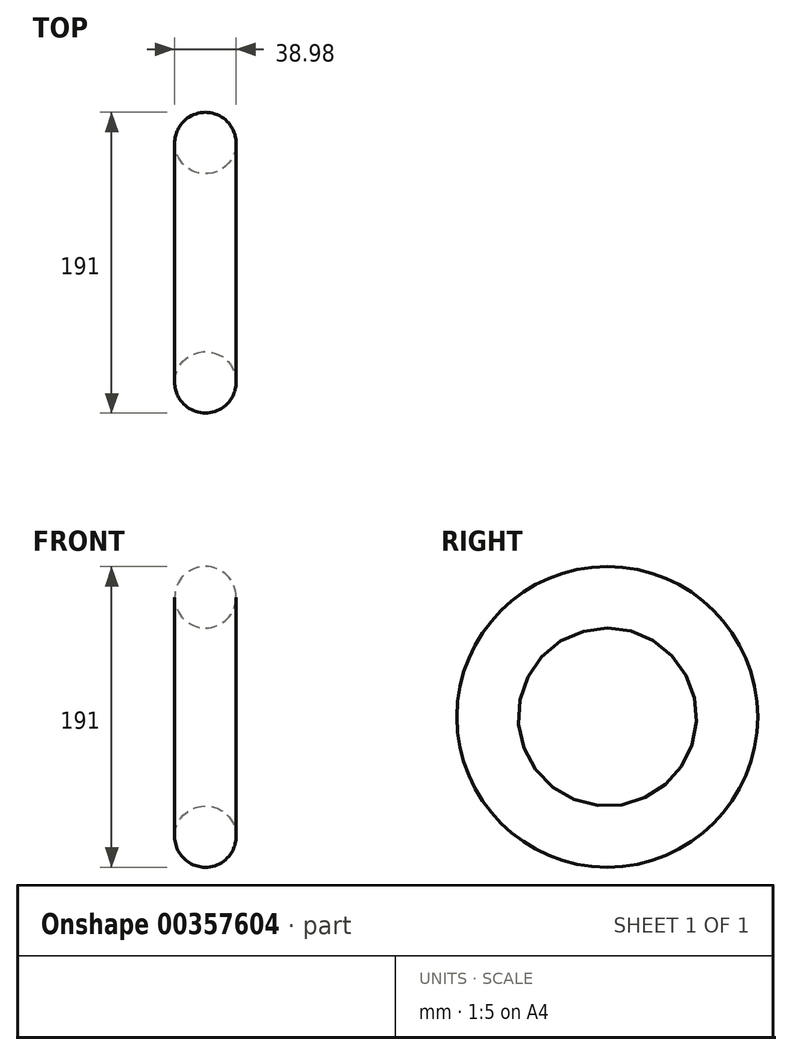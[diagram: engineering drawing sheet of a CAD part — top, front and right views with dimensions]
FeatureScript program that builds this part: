
annotation { "Feature Type Name" : "Feature", "Feature Type Description" : "" }
export const myFeature = defineFeature(function(context is Context, id is Id, definition is map)
    precondition{}
    {
        {
            var Q0;
            Q0=qCreatedBy(makeId("Front.planeOp"),FACE);
            var sketch = newSketch(context, id + "F0", { "sketchPlane" : qUnion([Q0])});
            skCircle(sketch, "E0", {"center": v(0, 0) * mm, "radius": 19.49 * mm});
            skLineSegment(sketch, "E1", {"start": v(-26.07, -76) * mm, "end": v(24.42, -76) * mm});
            skSolve(sketch);
        }
        {
            var Q0;
            Q0=makeQuery(id+"F0.imprint","IMPRINT",FACE,{"disambiguationData":[TD([[makeQuery(id+"F0.imprint","IMPRINT",EDGE,{"derivedFrom":sQuery(id+"F0.wireOp",EDGE,"E0")}),1.0]])]});
            var Q1;
            Q1=sQuery(id+"F0.wireOp",EDGE,"E1");
            revolve(context, id + "F1", {"entities" : qUnion([Q0]), "axis" : qUnion([Q1]), "revolveType" : RevolveType.FULL});
        }
    });
